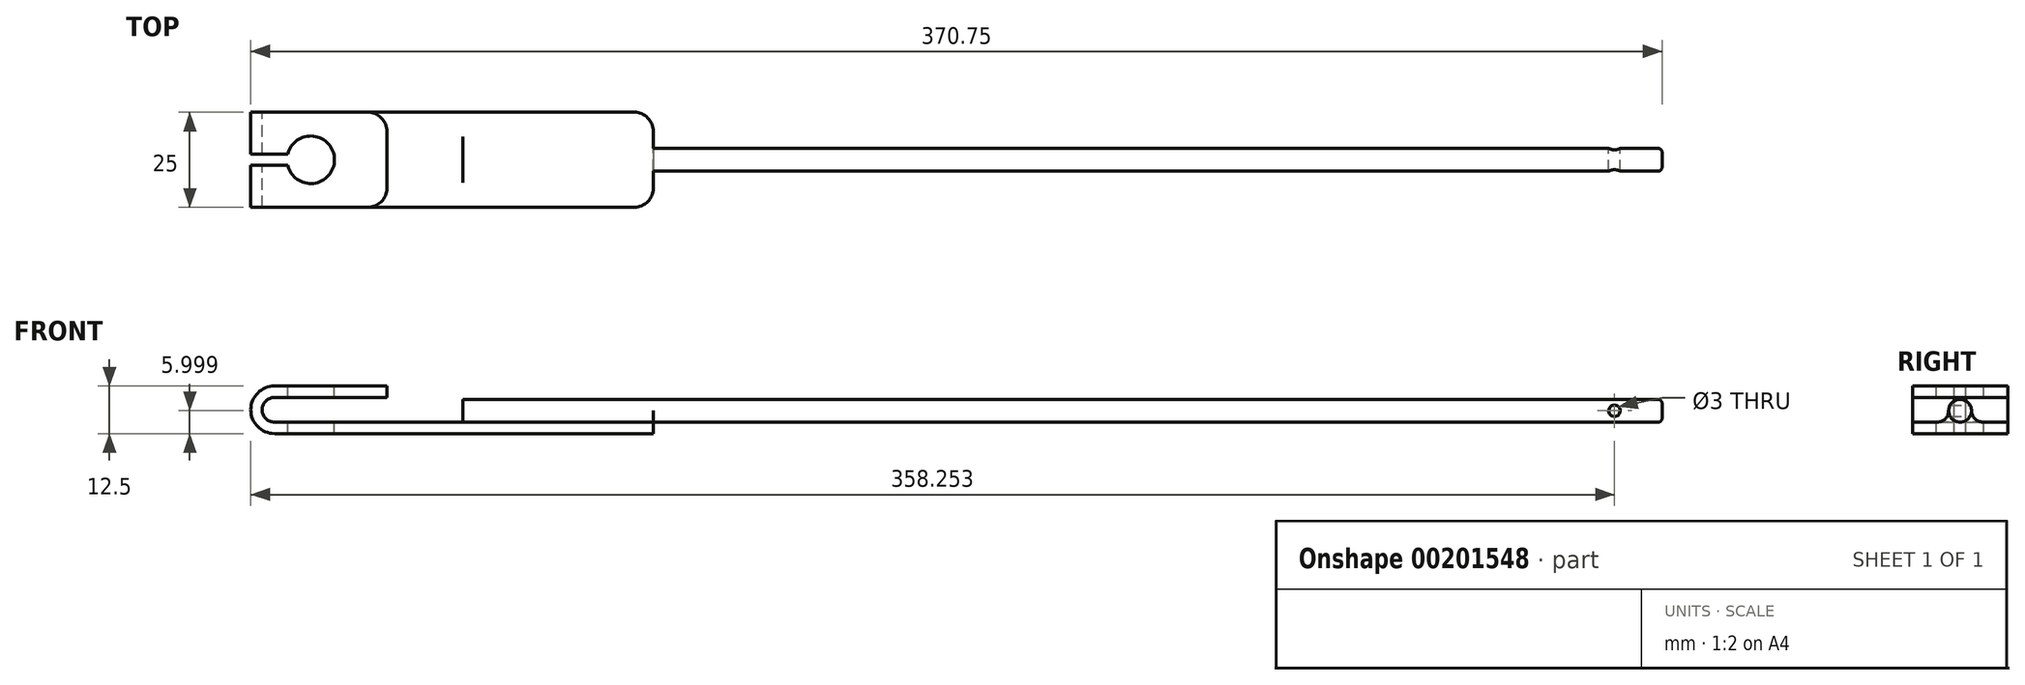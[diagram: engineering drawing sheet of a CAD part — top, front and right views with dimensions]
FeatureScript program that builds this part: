
annotation { "Feature Type Name" : "Feature", "Feature Type Description" : "" }
export const myFeature = defineFeature(function(context is Context, id is Id, definition is map)
    precondition{}
    {
        {
            var Q0;
            Q0=qCreatedBy(makeId("Front.planeOp"),FACE);
            var sketch = newSketch(context, id + "F0", { "sketchPlane" : qUnion([Q0])});
            skLineSegment(sketch, "E0", {"start": v(-35.59, -9.5) * mm, "end": v(63.91, -9.5) * mm});
            skLineSegment(sketch, "E1", {"start": v(63.91, -6.5) * mm, "end": v(-35.59, -6.5) * mm});
            skArc(sketch, "E2", {"start": v(-35.59, -6.5) * mm, "mid": v(-38.84, -3.25) * mm, "end": v(-35.59, 0) * mm});
            skLineSegment(sketch, "E3", {"start": v(-35.59, 0) * mm, "end": v(-6.09, 0) * mm});
            skLineSegment(sketch, "E4", {"start": v(-6.09, 3) * mm, "end": v(-35.59, 3) * mm});
            skArc(sketch, "E5", {"start": v(-35.59, -9.5) * mm, "mid": v(-41.84, -3.25) * mm, "end": v(-35.59, 3) * mm});
            skLineSegment(sketch, "E6", {"start": v(-26.09, 9.98) * mm, "end": v(-26.09, -27.42) * mm, "construction": true});
            skLineSegment(sketch, "E7", {"start": v(-6.09, 3) * mm, "end": v(-6.09, 0) * mm});
            skLineSegment(sketch, "E8", {"start": v(63.91, -6.5) * mm, "end": v(63.91, -9.5) * mm});
            skSolve(sketch);
        }
        {
            var Q0;
            Q0=makeQuery(id+"F0.imprint","IMPRINT",FACE,{"disambiguationData":[TD([[makeQuery(id+"F0.imprint","IMPRINT",EDGE,{"derivedFrom":sQuery(id+"F0.wireOp",EDGE,"E0")}),1.0]])]});
            extrude(context, id + "F1", {"entities" : qUnion([Q0]), "depth" : 25 * mm});
        }
        {
            var Q0;
            Q0=makeQuery(id+"F1.opExtrude","SWEPT_FACE",FACE,{"disambiguationData":[OSD([sQuery(id+"F0.wireOp",EDGE,"E4")])]});
            var sketch = newSketch(context, id + "F2", { "sketchPlane" : qUnion([Q0])});
            skLineSegment(sketch, "E9", {"start": v(-26.09, 9.17) * mm, "end": v(-26.09, -46.98) * mm, "construction": true});
            skLineSegment(sketch, "E10", {"start": v(-53.16, -12.5) * mm, "end": v(7.57, -12.5) * mm, "construction": true});
            skCircle(sketch, "E11", {"center": v(-26.09, -12.5) * mm, "radius": 6.25 * mm});
            skLineSegment(sketch, "E12", {"start": v(-32.15, -11) * mm, "end": v(-41.91, -11) * mm});
            skLineSegment(sketch, "E13", {"start": v(-32.15, -14) * mm, "end": v(-41.91, -14) * mm});
            skLineSegment(sketch, "E14", {"start": v(-41.91, -11) * mm, "end": v(-41.91, -14) * mm});
            skSolve(sketch);
        }
        {
            var Q0;
            Q0=makeQuery(id+"F2.imprint","IMPRINT",FACE,{"disambiguationData":[TD([[makeQuery(id+"F2.imprint","IMPRINT",EDGE,{"derivedFrom":sQuery(id+"F2.wireOp",EDGE,"E11")}),1.0]])]});
            extrude(context, id + "F3", {"entities" : qUnion([Q0]), "operationType" : NewBodyOperationType.REMOVE, "endBound" : BoundingType.THROUGH_ALL, "oppositeDirection" : true, "depth" : 25 * mm});
        }
        {
            var Q0;
            Q0 = qSketchRegion(id + "F2", true);
            extrude(context, id + "F4", {"entities" : qUnion([Q0]), "operationType" : NewBodyOperationType.REMOVE, "endBound" : BoundingType.THROUGH_ALL, "oppositeDirection" : true, "depth" : 25 * mm});
        }
        {
            var Q0;
            Q0=makeQuery(id+"F1.opExtrude","SWEPT_FACE",FACE,{"disambiguationData":[OSD([sQuery(id+"F0.wireOp",EDGE,"E8")])]});
            cPlane(context, id + "F5", {"entities" : qUnion([Q0]), "cplaneType" : CPlaneType.OFFSET, "offset" : 5 * mm, "oppositeDirection" : true, "width" : 150 * mm, "height" : 150 * mm});
        }
        {
            var Q0;
            Q0=qCreatedBy(id+"F5.planeOp",FACE);
            var sketch = newSketch(context, id + "F6", { "sketchPlane" : qUnion([Q0])});
            skLineSegment(sketch, "E15", {"start": v(-12.5, 1.43) * mm, "end": v(-12.5, -16.58) * mm, "construction": true});
            skLineSegment(sketch, "E16", {"start": v(-21.15, -3.5) * mm, "end": v(-3.79, -3.5) * mm, "construction": true});
            skCircle(sketch, "E17", {"center": v(-12.5, -3.5) * mm, "radius": 3 * mm});
            skLineSegment(sketch, "E18", {"start": v(-18.5, -6.5) * mm, "end": v(-6.5, -6.5) * mm});
            skSolve(sketch);
        }
        {
            var Q0;
            Q0 = qSketchRegion(id + "F6", true);
            extrude(context, id + "F7", {"entities" : qUnion([Q0]), "operationType" : NewBodyOperationType.ADD, "depth" : 270 * mm, "hasSecondDirection" : true, "secondDirectionOppositeDirection" : true, "secondDirectionDepth" : 45 * mm});
        }
        {
            var Q0;
            Q0=makeQuery(id+"F7.boolean.opBoolean","INTERSECT",EDGE,{"disambiguationData":[OD(1.0)],"derivedFrom":[makeQuery(id+"F1.opExtrude","SWEPT_FACE",FACE,{"disambiguationData":[OSD([sQuery(id+"F0.wireOp",EDGE,"E1")])]}),makeQuery(id+"F7.opExtrude","SWEPT_FACE",FACE,{"disambiguationData":[OSD([sQuery(id+"F6.wireOp",EDGE,"E17")])]})]});
            var Q1;
            Q1=makeQuery(id+"F7.boolean.opBoolean","INTERSECT",EDGE,{"disambiguationData":[OD(0.0)],"derivedFrom":[makeQuery(id+"F1.opExtrude","SWEPT_FACE",FACE,{"disambiguationData":[OSD([sQuery(id+"F0.wireOp",EDGE,"E1")])]}),makeQuery(id+"F7.opExtrude","SWEPT_FACE",FACE,{"disambiguationData":[OSD([sQuery(id+"F6.wireOp",EDGE,"E17")])]})]});
            fillet(context, id + "F8", {"entities" : qUnion([Q0, Q1]), "radius" : 3 * mm, "allowEdgeOverflow" : false});
        }
        {
            var Q0;
            Q0=makeQuery(id+"F1.opExtrude","CAP_EDGE",EDGE,{"disambiguationData":[OSD([sQuery(id+"F0.wireOp",EDGE,"E8")])],"isStart":false});
            var Q1;
            Q1=makeQuery(id+"F1.opExtrude","CAP_EDGE",EDGE,{"disambiguationData":[OSD([sQuery(id+"F0.wireOp",EDGE,"E8")])],"isStart":true});
            var Q2;
            Q2=makeQuery(id+"F1.opExtrude","CAP_EDGE",EDGE,{"disambiguationData":[OSD([sQuery(id+"F0.wireOp",EDGE,"E7")])],"isStart":true});
            var Q3;
            Q3=makeQuery(id+"F1.opExtrude","CAP_EDGE",EDGE,{"disambiguationData":[OSD([sQuery(id+"F0.wireOp",EDGE,"E7")])],"isStart":false});
            fillet(context, id + "F9", {"entities" : qUnion([Q0, Q1, Q2, Q3]), "radius" : 5 * mm, "tangentPropagation" : true, "allowEdgeOverflow" : false});
        }
        {
            var Q0;
            Q0=makeQuery(id+"F7.opExtrude","CAP_EDGE",EDGE,{"disambiguationData":[OSD([sQuery(id+"F6.wireOp",EDGE,"E17")])],"isStart":false});
            fillet(context, id + "F10", {"entities" : qUnion([Q0]), "radius" : 1 * mm, "tangentPropagation" : true, "allowEdgeOverflow" : false});
        }
        {
            var Q0;
            Q0=qCreatedBy(makeId("Front.planeOp"),FACE);
            var sketch = newSketch(context, id + "F11", { "sketchPlane" : qUnion([Q0])});
            skLineSegment(sketch, "E19", {"start": v(123.83, -3.5) * mm, "end": v(302.75, -3.5) * mm, "construction": true});
            skLineSegment(sketch, "E20", {"start": v(316.41, 6.04) * mm, "end": v(316.41, -24.68) * mm, "construction": true});
            skPoint(sketch, "E21", {"position": v(316.41, -3.5) * mm});
            skSolve(sketch);
        }
        {
            var Q0;
            Q0=sQuery(id+"F11.wireOp",VERTEX,"E21");
            var Q1;
            Q1=makeQuery(id+"F1.opExtrude","SWEPT_BODY",BODY,{"disambiguationData":[OSD([sQuery(id+"F0.wireOp",EDGE,"E0"),sQuery(id+"F0.wireOp",EDGE,"E1"),sQuery(id+"F0.wireOp",EDGE,"E2"),sQuery(id+"F0.wireOp",EDGE,"E3"),sQuery(id+"F0.wireOp",EDGE,"E4"),sQuery(id+"F0.wireOp",EDGE,"E5"),sQuery(id+"F0.wireOp",EDGE,"E7"),sQuery(id+"F0.wireOp",EDGE,"E8")])]});
            hole(context, id + "F12", {"style" : HoleStyle.SIMPLE, "endStyle" : HoleEndStyle.THROUGH, "oppositeDirection" : true, "holeDiameter" : 3 * mm, "locations" : qUnion([Q0]), "scope" : qUnion([Q1]), "isTappedThrough" : true});
        }
    });
